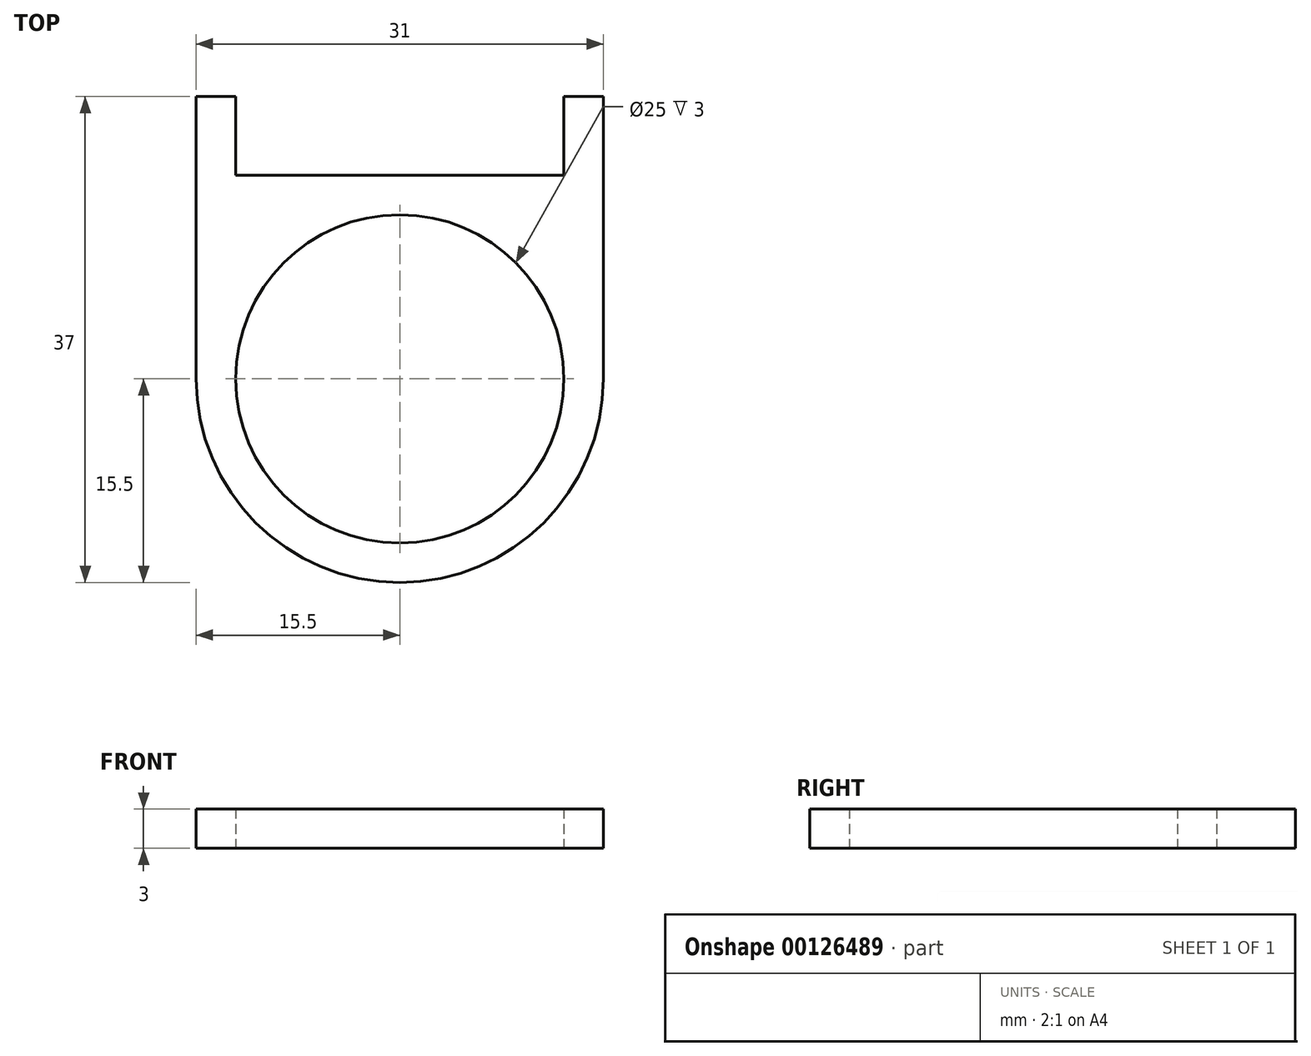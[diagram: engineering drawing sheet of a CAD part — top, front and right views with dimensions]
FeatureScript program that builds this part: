
annotation { "Feature Type Name" : "Feature", "Feature Type Description" : "" }
export const myFeature = defineFeature(function(context is Context, id is Id, definition is map)
    precondition{}
    {
        {
            var Q0;
            Q0=qCreatedBy(makeId("Top.planeOp"),FACE);
            var sketch = newSketch(context, id + "F0", { "sketchPlane" : qUnion([Q0])});
            skCircle(sketch, "E0", {"center": v(0, 0) * mm, "radius": 12.5 * mm});
            skArc(sketch, "E1.0", {"start": v(-15.5, 0) * mm, "mid": v(0, -15.5) * mm, "end": v(15.5, 0) * mm});
            skLineSegment(sketch, "E2", {"start": v(-15.5, 0) * mm, "end": v(-15.5, 15.5) * mm});
            skLineSegment(sketch, "E3", {"start": v(15.5, 0) * mm, "end": v(15.5, 15.5) * mm});
            skPoint(sketch, "E4.start.orphan", {"position": v(0, 15.5) * mm});
            skLineSegment(sketch, "E5", {"start": v(0, 0) * mm, "end": v(0, 24.6) * mm, "construction": true});
            skLineSegment(sketch, "E6", {"start": v(0, 15.5) * mm, "end": v(-12.5, 15.5) * mm});
            skLineSegment(sketch, "E7", {"start": v(0, 15.5) * mm, "end": v(12.5, 15.5) * mm});
            skLineSegment(sketch, "E8", {"start": v(-15.5, 15.5) * mm, "end": v(-15.5, 18.5) * mm});
            skLineSegment(sketch, "E9", {"start": v(-12.5, 18.5) * mm, "end": v(-12.5, 15.5) * mm});
            skLineSegment(sketch, "E10", {"start": v(15.5, 15.5) * mm, "end": v(15.5, 18.5) * mm});
            skLineSegment(sketch, "E11", {"start": v(12.5, 18.5) * mm, "end": v(12.5, 15.5) * mm});
            skLineSegment(sketch, "E12", {"start": v(-15.5, 18.5) * mm, "end": v(-15.5, 21.5) * mm});
            skLineSegment(sketch, "E13", {"start": v(-15.5, 21.5) * mm, "end": v(-12.5, 21.5) * mm});
            skLineSegment(sketch, "E14", {"start": v(-12.5, 21.5) * mm, "end": v(-12.5, 18.5) * mm});
            skLineSegment(sketch, "E15", {"start": v(12.5, 18.5) * mm, "end": v(12.5, 21.5) * mm});
            skLineSegment(sketch, "E16", {"start": v(12.5, 21.5) * mm, "end": v(15.5, 21.5) * mm});
            skLineSegment(sketch, "E17", {"start": v(15.5, 21.5) * mm, "end": v(15.5, 18.5) * mm});
            skSolve(sketch);
        }
        {
            var Q0;
            Q0=qSketchRegion(id+"F0",true);
            extrude(context, id + "F1", {"entities" : qUnion([Q0]), "endBound" : BoundingType.SYMMETRIC, "depth" : 3 * mm});
        }
    });
